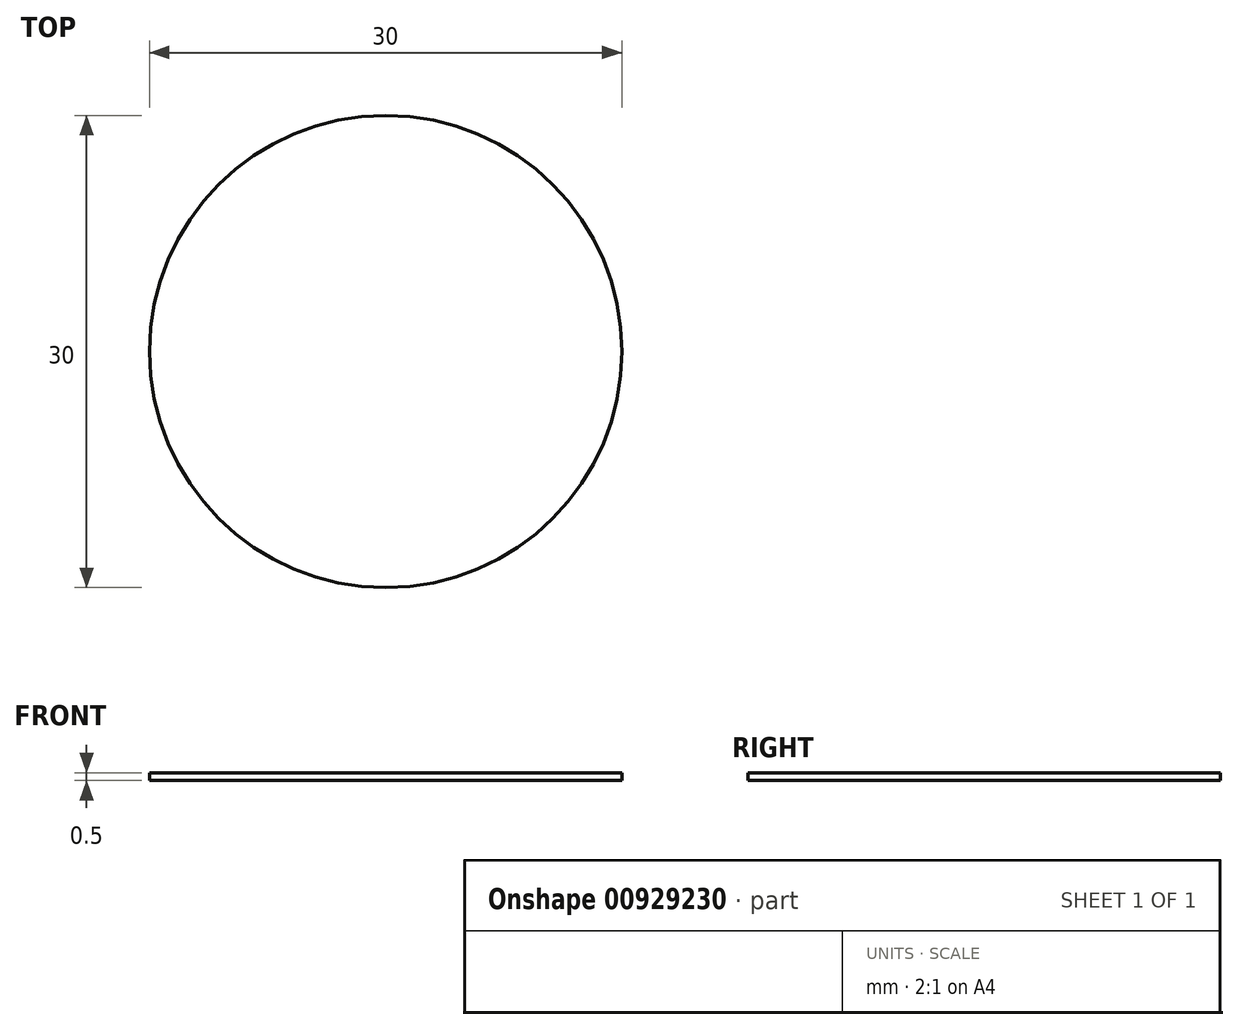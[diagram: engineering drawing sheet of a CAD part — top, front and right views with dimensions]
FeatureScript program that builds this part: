
annotation { "Feature Type Name" : "Feature", "Feature Type Description" : "" }
export const myFeature = defineFeature(function(context is Context, id is Id, definition is map)
    precondition{}
    {
        {
            var Q0;
            Q0=qCreatedBy(makeId("Top.planeOp"),FACE);
            var sketch = newSketch(context, id + "F0", { "sketchPlane" : qUnion([Q0])});
            skCircle(sketch, "E0", {"center": v(0, 0) * mm, "radius": 15 * mm});
            skSolve(sketch);
        }
        {
            var Q0;
            Q0=makeQuery(id+"F0.imprint","IMPRINT",FACE,{"disambiguationData":[TD([[makeQuery(id+"F0.imprint","IMPRINT",EDGE,{"derivedFrom":sQuery(id+"F0.wireOp",EDGE,"E0")}),1.0]])]});
            extrude(context, id + "F1", {"entities" : qUnion([Q0]), "depth" : 0.5 * mm, "offsetDistance" : 25.4 * mm});
        }
    });
